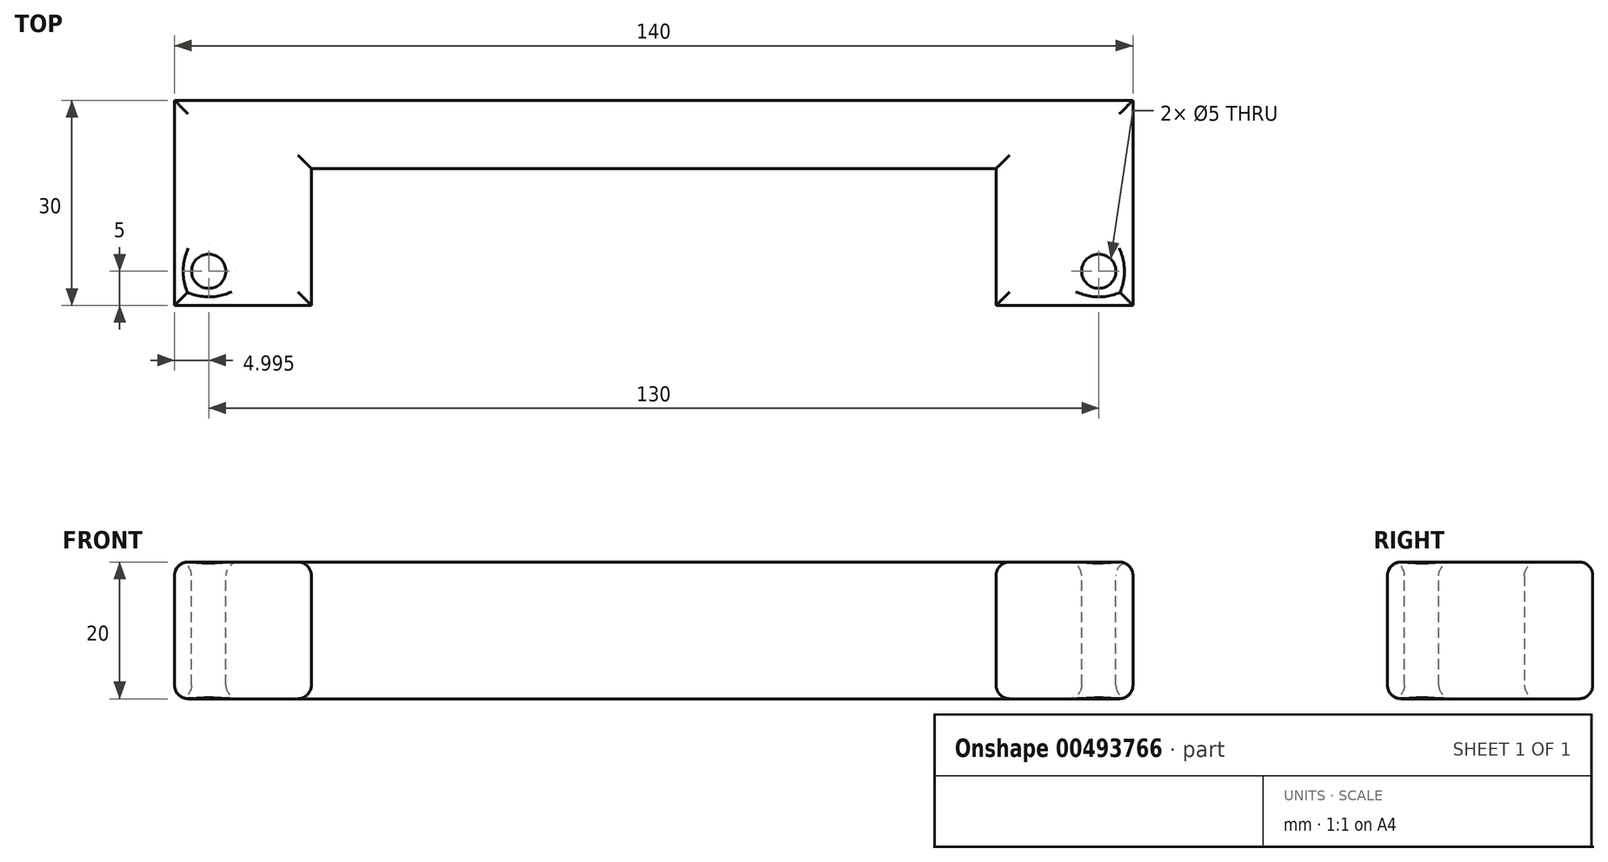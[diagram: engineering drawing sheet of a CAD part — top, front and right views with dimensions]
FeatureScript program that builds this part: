
annotation { "Feature Type Name" : "Feature", "Feature Type Description" : "" }
export const myFeature = defineFeature(function(context is Context, id is Id, definition is map)
    precondition{}
    {
        {
            var Q0;
            Q0=qCreatedBy(makeId("Top.planeOp"),FACE);
            var sketch = newSketch(context, id + "F0", { "sketchPlane" : qUnion([Q0])});
            skLineSegment(sketch, "E0", {"start": v(-24.5, 30) * mm, "end": v(-24.5, 20) * mm});
            skLineSegment(sketch, "E1", {"start": v(-24.5, 20) * mm, "end": v(25.5, 20) * mm});
            skLineSegment(sketch, "E2", {"start": v(25.5, 20) * mm, "end": v(25.5, 0) * mm});
            skLineSegment(sketch, "E3", {"start": v(25.5, 0) * mm, "end": v(45.5, 0) * mm});
            skLineSegment(sketch, "E4", {"start": v(45.5, 0) * mm, "end": v(45.5, 30) * mm});
            skLineSegment(sketch, "E5", {"start": v(45.5, 30) * mm, "end": v(-24.5, 30) * mm});
            skSolve(sketch);
        }
        {
            var Q0;
            Q0=makeQuery(id+"F0.imprint","IMPRINT",FACE,{"disambiguationData":[TD([[makeQuery(id+"F0.imprint","IMPRINT",EDGE,{"derivedFrom":sQuery(id+"F0.wireOp",EDGE,"E0")}),1.0]])]});
            extrude(context, id + "F1", {"entities" : qUnion([Q0]), "depth" : 20 * mm});
        }
        {
            var Q0;
            Q0=makeQuery(id+"F1.opExtrude","CAP_FACE",FACE,{"disambiguationData":[OSD([sQuery(id+"F0.wireOp",EDGE,"E0"),sQuery(id+"F0.wireOp",EDGE,"E1"),sQuery(id+"F0.wireOp",EDGE,"E2"),sQuery(id+"F0.wireOp",EDGE,"E3"),sQuery(id+"F0.wireOp",EDGE,"E4"),sQuery(id+"F0.wireOp",EDGE,"E5")])],"isStart":false});
            var sketch = newSketch(context, id + "F2", { "sketchPlane" : qUnion([Q0])});
            skPoint(sketch, "E6", {"position": v(40.5, 5) * mm});
            skSolve(sketch);
        }
        {
            var Q0;
            Q0=sQuery(id+"F2.wireOp",VERTEX,"E6");
            var Q1;
            Q1=makeQuery(id+"F1.opExtrude","SWEPT_BODY",BODY,{"disambiguationData":[OSD([sQuery(id+"F0.wireOp",EDGE,"E0"),sQuery(id+"F0.wireOp",EDGE,"E1"),sQuery(id+"F0.wireOp",EDGE,"E2"),sQuery(id+"F0.wireOp",EDGE,"E3"),sQuery(id+"F0.wireOp",EDGE,"E4"),sQuery(id+"F0.wireOp",EDGE,"E5")])]});
            hole(context, id + "F3", {"style" : HoleStyle.SIMPLE, "endStyle" : HoleEndStyle.THROUGH, "holeDiameter" : 5 * mm, "isTappedThrough" : true, "tappedDepth" : 12 * mm, "tapClearance" : 3, "locations" : qUnion([Q0]), "scope" : qUnion([Q1])});
        }
        {
            var Q0;
            Q0=makeQuery(id+"F1.opExtrude","SWEPT_BODY",BODY,{"disambiguationData":[OSD([sQuery(id+"F0.wireOp",EDGE,"E0"),sQuery(id+"F0.wireOp",EDGE,"E1"),sQuery(id+"F0.wireOp",EDGE,"E2"),sQuery(id+"F0.wireOp",EDGE,"E3"),sQuery(id+"F0.wireOp",EDGE,"E4"),sQuery(id+"F0.wireOp",EDGE,"E5")])]});
            var Q1;
            Q1=makeQuery(id+"F1.opExtrude","SWEPT_FACE",FACE,{"disambiguationData":[OSD([sQuery(id+"F0.wireOp",EDGE,"E0")])]});
            mirror(context, id + "F4", {"operationType" : NewBodyOperationType.ADD, "entities" : qUnion([Q0]), "mirrorPlane" : qUnion([Q1])});
        }
        {
            var Q0;
            {var subQ0=makeQuery(id+"F1.opExtrude","CAP_FACE",FACE,{"disambiguationData":[OSD([sQuery(id+"F0.wireOp",EDGE,"E0"),sQuery(id+"F0.wireOp",EDGE,"E1"),sQuery(id+"F0.wireOp",EDGE,"E2"),sQuery(id+"F0.wireOp",EDGE,"E3"),sQuery(id+"F0.wireOp",EDGE,"E4"),sQuery(id+"F0.wireOp",EDGE,"E5")])],"isStart":false});Q0=makeQuery(id+"F4.boolean.opBoolean","MERGE",FACE,{"derivedFrom":[subQ0,makeQuery(id+"F4.opPattern","COPY",FACE,{"derivedFrom":subQ0,"instanceName":"1"})]});}
            var Q1;
            {var subQ0=makeQuery(id+"F1.opExtrude","CAP_FACE",FACE,{"disambiguationData":[OSD([sQuery(id+"F0.wireOp",EDGE,"E0"),sQuery(id+"F0.wireOp",EDGE,"E1"),sQuery(id+"F0.wireOp",EDGE,"E2"),sQuery(id+"F0.wireOp",EDGE,"E3"),sQuery(id+"F0.wireOp",EDGE,"E4"),sQuery(id+"F0.wireOp",EDGE,"E5")])],"isStart":true});Q1=makeQuery(id+"F4.boolean.opBoolean","MERGE",FACE,{"derivedFrom":[subQ0,makeQuery(id+"F4.opPattern","COPY",FACE,{"derivedFrom":subQ0,"instanceName":"1"})]});}
            fillet(context, id + "F5", {"entities" : qUnion([Q0, Q1]), "radius" : 2 * mm, "tangentPropagation" : true, "allowEdgeOverflow" : false});
        }
    });
